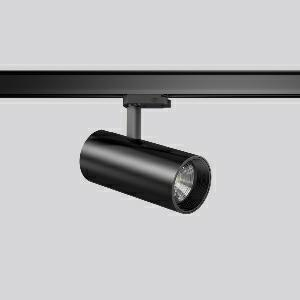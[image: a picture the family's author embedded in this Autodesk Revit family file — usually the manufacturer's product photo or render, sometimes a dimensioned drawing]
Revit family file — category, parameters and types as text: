
# Revit family: deecos_s_mini_742201_003_76_3193
name_source: partatom
category: Lighting Fixtures
units: mm (PartAtom-declared; Revit-internal decimal feet)

## family parameters
Cut with Voids When Loaded = No
Host = Face
Light Source = No
Part Type = Normal
Room Calculation Point = No
Round Connector Dimension = Use Diameter
Shared = No

## types (1)
- DEECOS S mini (1 x LED Modul 930, 2250 lm, 3000)
    Apparent Load = 20 VA
    Approval mark = CE
    CIE Flux Codes = 80 99 100 100 100
    Color Rendering = 90
    Color Temperature = 3000
    Default Elevation = 1800 mm
    Description = Series: DEECOS S mini
LED surface-mounted projector in modern design with no visible cooling ribs. Housing: die-cast aluminium, powder-coated. Rotation range: 356°. Swivel range: 90°. Black plastic ring and recessed LED to prevent glare from the side. Optical assembly with lens made of plastic (polycarbonate) for the best homogeneous light distribution - can be changed without tools. Best colour rendering index Ra>90. With adapter for RZB 3-circuit DALI tracks. Suitable for Track on ceiling, Wall track. High quality converter without flickering and stroboscopic effect. The following accessories can be mounted without use of tools: interchangeable lenses, decorative glasses, honeycomb louvre, clear and frosted diffusers, white interchangeable plastic ring. 
Colour: deep black, matt (RAL 9005)
Diameter: 87 mm
Height: 214 mm
Lamp: LED
Socket: without socket
Colour temperature: 3000K
Colour rendering index (CRI): 92
System power: 20 W
Rated luminous flux: 2250 lm
Luminous efficiency: 113 lm/W
Control gear: Converter, dimmable, DALI
Protection class: I
Type of protection: IP 20
    Height = 214 mm
    Lamp = 1 x LED Modul 930
    Lamp Light Flux = 2250 lm
    Lamp count = 1
    Length = 87 mm
    Lifetime = 50000 h
    Luminous efficacy = 113 lm/W
    Manufacturer = RZB
    ModVariant = No
    Model = 742201.003.76
    Mounting Place = Ceiling
    Mounting Type = Rail mounted
    Number of Poles = 1
    OnlyDefault = Yes
    Power Factor = 1
    Product Name = DEECOS S mini
    Product group = Track mounted projectors
    ProductGroupID = 301
    Protection Class = Protection class I
    Protection Degree = IP 20
    RLX_Detail_Level = 1
    RLX_Emergency_Light_Flux = 0 lm
    RLX_Emergency_Type = 0
    RLX_Emergency_Type_DB = No
    RlxData = <blob elided: 39249 chars, md5=c802391c>
    Socket = socket
    Standby Power = 0 W
    System Light Flux = 2250 lm
    System Power = 20 W
    Type Comments = Product without accessories
    Type Image = 741930.003.jpg
    URL = http://relux.com
    VarID = ---
    Voltage = 230 V
    Voltage Range = 220-240 V
    Weight = 0.00 kg
    Width = 0 mm  [stored 0 ft]

note: [stored X ft] marks values corroborated as IEEE doubles in the binary element streams (Revit-internal decimal feet)

## geometry (parser evidence)
native form markers: Blend x4, Sweep x12
no freeform markers — native parametric forms only
